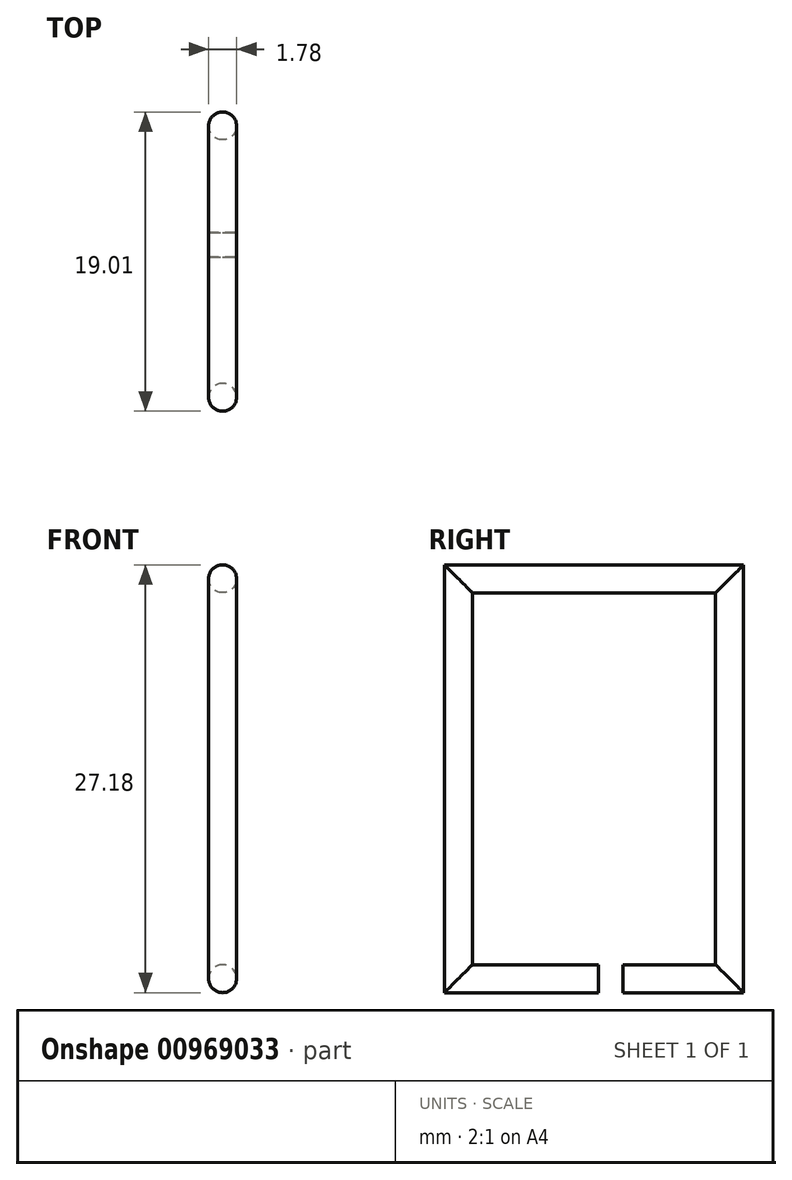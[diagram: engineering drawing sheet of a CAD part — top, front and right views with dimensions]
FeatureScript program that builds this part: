
annotation { "Feature Type Name" : "Feature", "Feature Type Description" : "" }
export const myFeature = defineFeature(function(context is Context, id is Id, definition is map)
    precondition{}
    {
        {
            var Q0;
            Q0=qCreatedBy(makeId("Front.planeOp"),FACE);
            var sketch = newSketch(context, id + "F0", { "sketchPlane" : qUnion([Q0])});
            skCircle(sketch, "E0", {"center": v(0, 0) * mm, "radius": 0.89 * mm});
            skSolve(sketch);
        }
        {
            var Q0;
            Q0=qCreatedBy(makeId("Right.planeOp"),FACE);
            var sketch = newSketch(context, id + "F1", { "sketchPlane" : qUnion([Q0])});
            skLineSegment(sketch, "E1", {"start": v(0, 0) * mm, "end": v(-8.89, 0) * mm});
            skLineSegment(sketch, "E2", {"start": v(-8.9, 25.4) * mm, "end": v(8.34, 25.4) * mm});
            skLineSegment(sketch, "E3", {"start": v(8.34, 25.4) * mm, "end": v(8.34, 0) * mm});
            skLineSegment(sketch, "E4", {"start": v(-8.9, 25.4) * mm, "end": v(-8.9, 0) * mm});
            skLineSegment(sketch, "E5", {"start": v(8.34, 0) * mm, "end": v(1.58, 0) * mm});
            skSolve(sketch);
        }
        {
            var Q0;
            Q0=makeQuery(id+"F0.imprint","IMPRINT",FACE,{"disambiguationData":[TD([[makeQuery(id+"F0.imprint","IMPRINT",EDGE,{"derivedFrom":sQuery(id+"F0.wireOp",EDGE,"E0")}),1.0]])]});
            var Q1;
            Q1=sQuery(id+"F1.wireOp",EDGE,"E1");
            var Q2;
            Q2=sQuery(id+"F1.wireOp",EDGE,"E4");
            var Q3;
            Q3=sQuery(id+"F1.wireOp",EDGE,"E2");
            var Q4;
            Q4=sQuery(id+"F1.wireOp",EDGE,"E3");
            var Q5;
            Q5=sQuery(id+"F1.wireOp",EDGE,"E5");
            sweep(context, id + "F2", {"profiles" : qUnion([Q0]), "path" : qUnion([Q1, Q2, Q3, Q4, Q5])});
        }
    });
